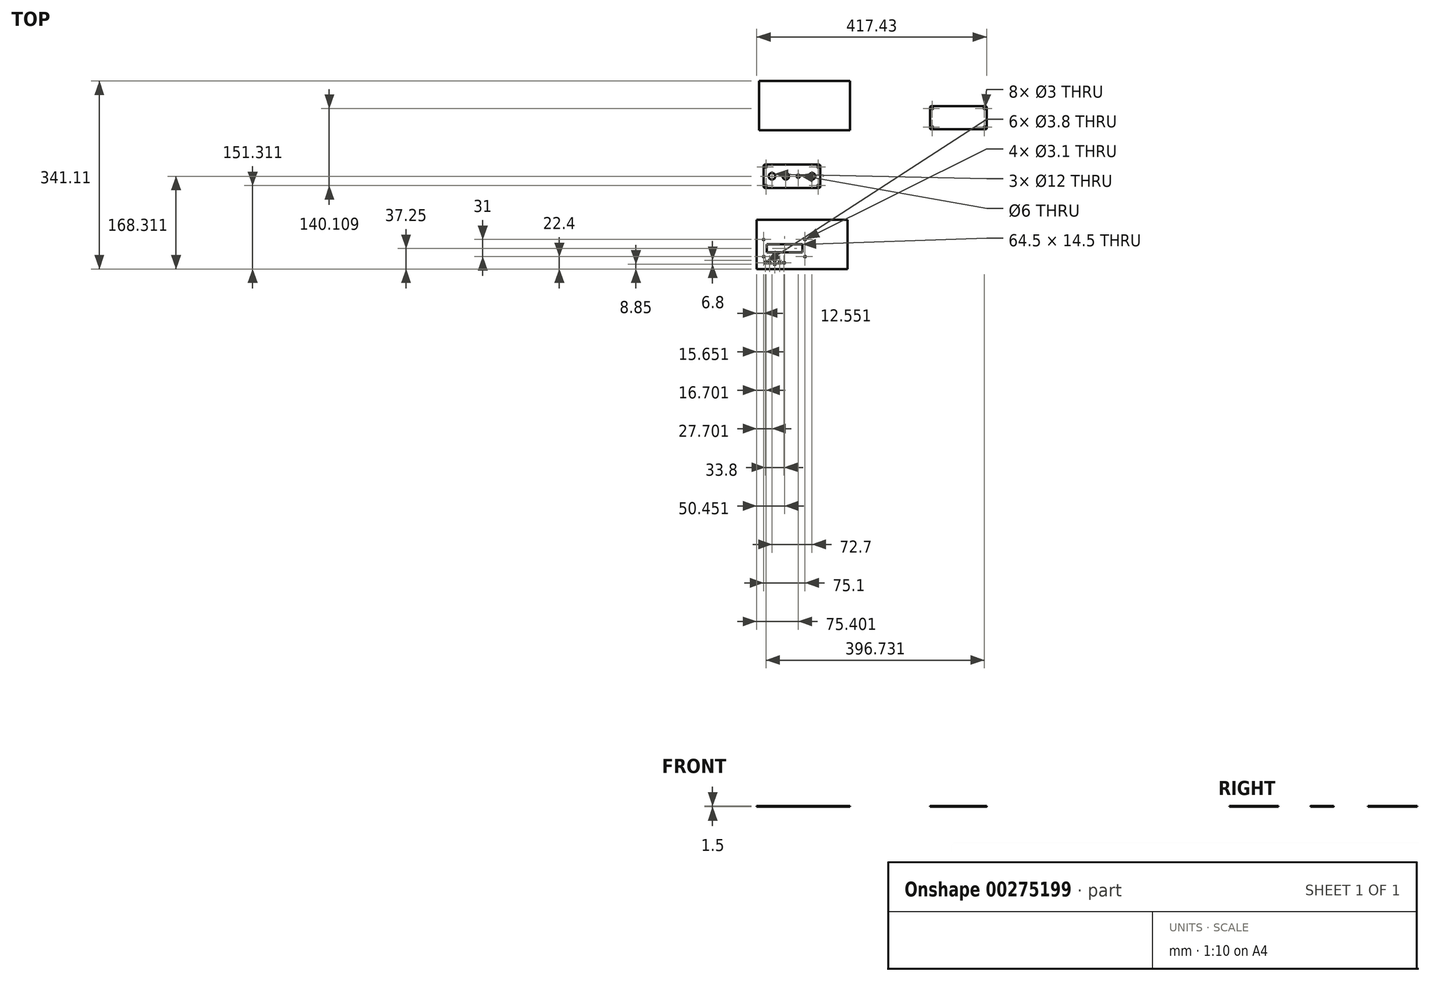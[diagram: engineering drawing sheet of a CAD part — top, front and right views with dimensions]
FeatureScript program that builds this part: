
annotation { "Feature Type Name" : "Feature", "Feature Type Description" : "" }
export const myFeature = defineFeature(function(context is Context, id is Id, definition is map)
    precondition{}
    {
        {
            var Q0;
            Q0=qCreatedBy(makeId("Top.planeOp"),FACE);
            var sketch = newSketch(context, id + "F0", { "sketchPlane" : qUnion([Q0])});
            skPoint(sketch, "E0", {"position": v(-55.37, -22.64) * mm});
            skPoint(sketch, "E1", {"position": v(-21.57, -22.64) * mm});
            skPoint(sketch, "E2", {"position": v(-47.47, -22.64) * mm});
            skPoint(sketch, "E3", {"position": v(-29.47, -22.64) * mm});
            skPoint(sketch, "E4", {"position": v(-38.32, -18.24) * mm});
            skPoint(sketch, "E5", {"position": v(-38.32, -25.04) * mm});
            skLineSegment(sketch, "E6", {"start": v(-55.37, -22.64) * mm, "end": v(-21.57, -22.64) * mm, "construction": true});
            skPoint(sketch, "E7", {"position": v(-58.47, 19.51) * mm});
            skPoint(sketch, "E8", {"position": v(16.63, 19.51) * mm});
            skPoint(sketch, "E9", {"position": v(-58.47, -11.49) * mm});
            skPoint(sketch, "E10", {"position": v(16.63, -11.49) * mm});
            skLineSegment(sketch, "E11", {"start": v(-61.02, 29.41) * mm, "end": v(-61.02, -28.89) * mm});
            skLineSegment(sketch, "E12", {"start": v(-61.02, 29.41) * mm, "end": v(19.08, 29.41) * mm});
            skLineSegment(sketch, "E13", {"start": v(-61.02, -28.89) * mm, "end": v(19.08, -28.89) * mm});
            skLineSegment(sketch, "E14", {"start": v(19.08, -28.89) * mm, "end": v(19.08, 29.41) * mm, "construction": true});
            skLineSegment(sketch, "E15.bottom", {"start": v(-52.82, 10.61) * mm, "end": v(11.68, 10.61) * mm});
            skLineSegment(sketch, "E15.top", {"start": v(-52.82, -3.89) * mm, "end": v(11.68, -3.89) * mm});
            skLineSegment(sketch, "E15.left", {"start": v(-52.82, 10.61) * mm, "end": v(-52.82, -3.89) * mm});
            skLineSegment(sketch, "E15.right", {"start": v(11.68, 10.61) * mm, "end": v(11.68, -3.89) * mm});
            skCircle(sketch, "E16", {"center": v(-55.37, -22.64) * mm, "radius": 1.9 * mm});
            skCircle(sketch, "E17", {"center": v(-47.47, -22.64) * mm, "radius": 1.9 * mm});
            skCircle(sketch, "E18", {"center": v(-38.32, -18.24) * mm, "radius": 1.9 * mm});
            skCircle(sketch, "E19", {"center": v(-38.32, -25.04) * mm, "radius": 1.9 * mm});
            skCircle(sketch, "E20", {"center": v(-29.47, -22.64) * mm, "radius": 1.9 * mm});
            skCircle(sketch, "E21", {"center": v(-21.57, -22.64) * mm, "radius": 1.9 * mm});
            skCircle(sketch, "E22", {"center": v(-58.47, 19.51) * mm, "radius": 1.55 * mm});
            skCircle(sketch, "E23", {"center": v(-58.47, -11.49) * mm, "radius": 1.55 * mm});
            skCircle(sketch, "E24", {"center": v(16.63, 19.51) * mm, "radius": 1.55 * mm});
            skCircle(sketch, "E25", {"center": v(16.63, -11.49) * mm, "radius": 1.55 * mm});
            skLineSegment(sketch, "E26.bottom", {"start": v(-71.02, 55.21) * mm, "end": v(93.98, 55.21) * mm});
            skLineSegment(sketch, "E26.top", {"start": v(-71.02, -33.89) * mm, "end": v(93.98, -33.89) * mm});
            skLineSegment(sketch, "E26.left", {"start": v(-71.02, 55.21) * mm, "end": v(-71.02, -33.89) * mm});
            skLineSegment(sketch, "E26.right", {"start": v(93.98, 55.21) * mm, "end": v(93.98, -33.89) * mm});
            skLineSegment(sketch, "E27.bottom", {"start": v(-61.02, -28.89) * mm, "end": v(53.98, -28.89) * mm, "construction": true});
            skLineSegment(sketch, "E27.top", {"start": v(-61.02, 29.41) * mm, "end": v(53.98, 29.41) * mm, "construction": true});
            skLineSegment(sketch, "E27.left", {"start": v(-61.02, -28.89) * mm, "end": v(-61.02, 29.41) * mm, "construction": true});
            skLineSegment(sketch, "E27.right", {"start": v(53.98, -28.89) * mm, "end": v(53.98, 29.41) * mm, "construction": true});
            skLineSegment(sketch, "E28.bottom", {"start": v(-56.32, 155.42) * mm, "end": v(42.38, 155.42) * mm});
            skLineSegment(sketch, "E28.top", {"start": v(-56.32, 113.42) * mm, "end": v(42.38, 113.42) * mm});
            skLineSegment(sketch, "E28.left", {"start": v(-58.32, 153.42) * mm, "end": v(-58.32, 115.42) * mm});
            skLineSegment(sketch, "E28.right", {"start": v(44.38, 153.42) * mm, "end": v(44.38, 115.42) * mm});
            skLineSegment(sketch, "E29", {"start": v(-58.32, 134.42) * mm, "end": v(44.38, 134.42) * mm, "construction": true});
            skCircle(sketch, "E30", {"center": v(-43.32, 134.42) * mm, "radius": 6 * mm});
            skCircle(sketch, "E31", {"center": v(-18.32, 134.42) * mm, "radius": 6 * mm});
            skCircle(sketch, "E32", {"center": v(29.38, 134.42) * mm, "radius": 6 * mm});
            skCircle(sketch, "E33", {"center": v(4.38, 134.42) * mm, "radius": 3 * mm});
            skPoint(sketch, "E34.visualSharp", {"position": v(-58.32, 155.42) * mm});
            skArc(sketch, "E34.filletArc", {"start": v(-56.32, 155.42) * mm, "mid": v(-57.73, 154.84) * mm, "end": v(-58.32, 153.42) * mm});
            skPoint(sketch, "E35.visualSharp", {"position": v(44.38, 155.42) * mm});
            skArc(sketch, "E35.filletArc", {"start": v(44.38, 153.42) * mm, "mid": v(43.8, 154.84) * mm, "end": v(42.38, 155.42) * mm});
            skPoint(sketch, "E36.visualSharp", {"position": v(44.38, 113.42) * mm});
            skArc(sketch, "E36.filletArc", {"start": v(42.38, 113.42) * mm, "mid": v(43.8, 114) * mm, "end": v(44.38, 115.42) * mm});
            skPoint(sketch, "E37.visualSharp", {"position": v(-58.32, 113.42) * mm});
            skArc(sketch, "E37.filletArc", {"start": v(-58.32, 115.42) * mm, "mid": v(-57.73, 114) * mm, "end": v(-56.32, 113.42) * mm});
            skLineSegment(sketch, "E38", {"start": v(-58.32, 151.42) * mm, "end": v(44.38, 151.42) * mm, "construction": true});
            skLineSegment(sketch, "E39", {"start": v(-54.32, 155.42) * mm, "end": v(-54.32, 113.42) * mm, "construction": true});
            skLineSegment(sketch, "E40", {"start": v(40.38, 155.42) * mm, "end": v(40.38, 113.42) * mm, "construction": true});
            skCircle(sketch, "E41", {"center": v(-54.32, 151.42) * mm, "radius": 1.5 * mm});
            skCircle(sketch, "E42", {"center": v(40.38, 151.42) * mm, "radius": 1.5 * mm});
            skCircle(sketch, "E43.MirrorC", {"center": v(40.38, 117.42) * mm, "radius": 1.5 * mm});
            skCircle(sketch, "E44.MirrorC", {"center": v(-54.32, 117.42) * mm, "radius": 1.5 * mm});
            skLineSegment(sketch, "E45.bottom", {"start": v(-66.87, 307.22) * mm, "end": v(98.13, 307.22) * mm});
            skLineSegment(sketch, "E45.top", {"start": v(-66.87, 218.12) * mm, "end": v(98.13, 218.12) * mm});
            skLineSegment(sketch, "E45.left", {"start": v(-66.87, 307.22) * mm, "end": v(-66.87, 218.12) * mm});
            skLineSegment(sketch, "E45.right", {"start": v(98.13, 307.22) * mm, "end": v(98.13, 218.12) * mm});
            skLineSegment(sketch, "E46.bottom", {"start": v(245.71, 261.53) * mm, "end": v(344.41, 261.53) * mm});
            skLineSegment(sketch, "E46.top", {"start": v(245.71, 219.53) * mm, "end": v(344.41, 219.53) * mm});
            skLineSegment(sketch, "E46.left", {"start": v(243.71, 259.53) * mm, "end": v(243.71, 221.53) * mm});
            skLineSegment(sketch, "E46.right", {"start": v(346.41, 259.53) * mm, "end": v(346.41, 221.53) * mm});
            skPoint(sketch, "E47.visualSharp", {"position": v(243.71, 261.53) * mm});
            skArc(sketch, "E47.filletArc", {"start": v(245.71, 261.53) * mm, "mid": v(244.3, 260.94) * mm, "end": v(243.71, 259.53) * mm});
            skPoint(sketch, "E48.visualSharp", {"position": v(346.41, 261.53) * mm});
            skArc(sketch, "E48.filletArc", {"start": v(346.41, 259.53) * mm, "mid": v(345.83, 260.94) * mm, "end": v(344.41, 261.53) * mm});
            skPoint(sketch, "E49.visualSharp", {"position": v(346.41, 219.53) * mm});
            skArc(sketch, "E49.filletArc", {"start": v(344.41, 219.53) * mm, "mid": v(345.83, 220.12) * mm, "end": v(346.41, 221.53) * mm});
            skPoint(sketch, "E50.visualSharp", {"position": v(243.71, 219.53) * mm});
            skArc(sketch, "E50.filletArc", {"start": v(243.71, 221.53) * mm, "mid": v(244.3, 220.12) * mm, "end": v(245.71, 219.53) * mm});
            skLineSegment(sketch, "E51", {"start": v(243.71, 257.53) * mm, "end": v(346.41, 257.53) * mm, "construction": true});
            skLineSegment(sketch, "E52", {"start": v(243.71, 240.53) * mm, "end": v(346.41, 240.53) * mm, "construction": true});
            skLineSegment(sketch, "E53", {"start": v(247.71, 261.53) * mm, "end": v(247.71, 219.53) * mm, "construction": true});
            skLineSegment(sketch, "E54", {"start": v(295.06, 261.53) * mm, "end": v(295.06, 219.53) * mm, "construction": true});
            skCircle(sketch, "E55", {"center": v(247.71, 257.53) * mm, "radius": 1.5 * mm});
            skCircle(sketch, "E56.MirrorC", {"center": v(342.41, 257.53) * mm, "radius": 1.5 * mm});
            skCircle(sketch, "E57.MirrorC", {"center": v(342.41, 223.53) * mm, "radius": 1.5 * mm});
            skCircle(sketch, "E58.MirrorC", {"center": v(247.71, 223.53) * mm, "radius": 1.5 * mm});
            skSolve(sketch);
        }
        {
            var Q0;
            Q0=makeQuery(id+"F0.imprint","IMPRINT",FACE,{"disambiguationData":[TD([[makeQuery(id+"F0.imprint","IMPRINT",EDGE,{"derivedFrom":sQuery(id+"F0.wireOp",EDGE,"E28.bottom")}),-1.0]])]});
            var Q1;
            Q1=makeQuery(id+"F0.imprint","IMPRINT",FACE,{"disambiguationData":[TD([[makeQuery(id+"F0.imprint","IMPRINT",EDGE,{"derivedFrom":sQuery(id+"F0.wireOp",EDGE,"E15.bottom")}),1.0]])]});
            var Q2;
            Q2=makeQuery(id+"F0.imprint","IMPRINT",FACE,{"disambiguationData":[TD([[makeQuery(id+"F0.imprint","IMPRINT",EDGE,{"derivedFrom":sQuery(id+"F0.wireOp",EDGE,"E45.bottom")}),-1.0]])]});
            var Q3;
            Q3=makeQuery(id+"F0.imprint","IMPRINT",FACE,{"disambiguationData":[TD([[makeQuery(id+"F0.imprint","IMPRINT",EDGE,{"derivedFrom":sQuery(id+"F0.wireOp",EDGE,"E46.bottom")}),-1.0]])]});
            extrude(context, id + "F1", {"entities" : qUnion([Q0, Q1, Q2, Q3]), "depth" : 1.5 * mm});
        }
    });
